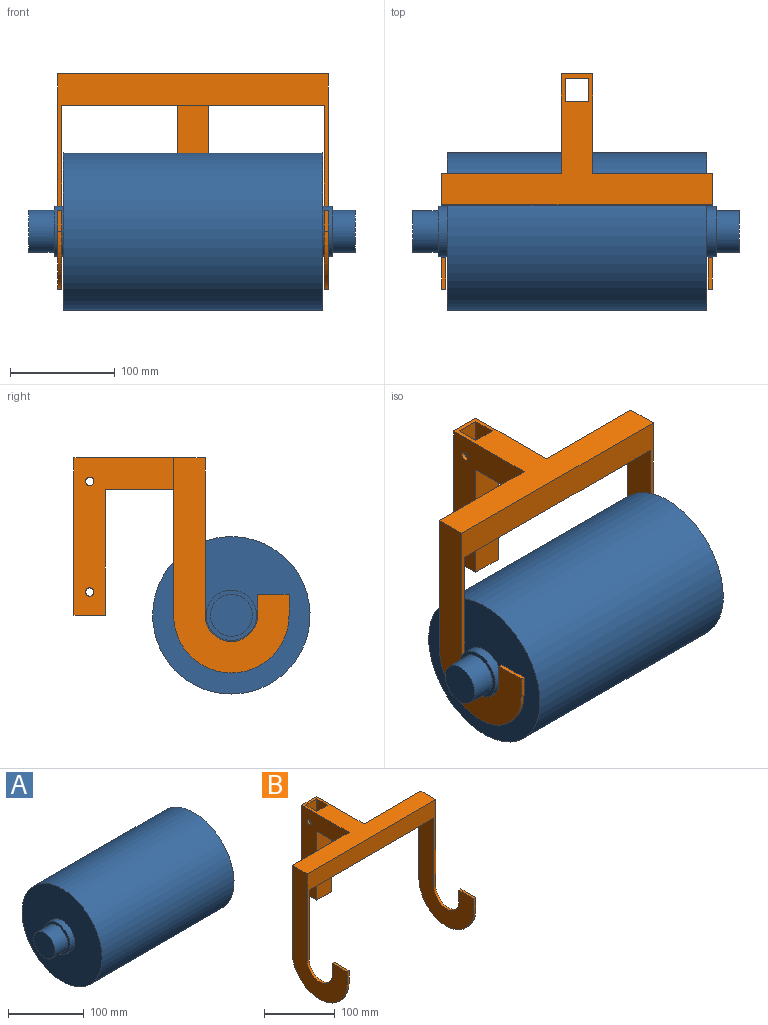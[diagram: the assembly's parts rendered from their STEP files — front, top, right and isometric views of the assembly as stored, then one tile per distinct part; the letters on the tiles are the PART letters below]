
ASSEMBLY  parts=2 mates=1
PART A: 11 faces, bbox 311x150x150 mm
  f0: cylinder r=75mm len=247mm, axis (-1,0,0), area 116396mm2, adj f1,f2
  f1: plane 150x150mm, normal (1,0,0), area 15861.9mm2, adj f0,f3
  f2: plane 150x150mm, normal (-1,0,0), area 15861.9mm2, adj f0,f7
  f3: cylinder r=24mm len=48mm, axis (-1,0,0), area 1357.2mm2, adj f1,f4
  f4: plane 48x48mm, normal (1,0,0), area 552.9mm2, adj f3,f5
  f5: cylinder r=20mm len=40mm, axis (-1,0,0), area 2764.6mm2, adj f4,f6
  f6: plane 40x40mm, normal (1,0,0), area 1256.6mm2, adj f5
  f7: cylinder r=24mm len=48mm, axis (1,0,0), area 1357.2mm2, adj f2,f8
  f8: plane 48x48mm, normal (-1,0,0), area 552.9mm2, adj f7,f9
  f9: cylinder r=20mm len=40mm, axis (1,0,0), area 3015.9mm2, adj f8,f10
  f10: plane 40x40mm, normal (-1,0,0), area 1256.6mm2, adj f9
PART B: 44 faces, bbox 258x205x205 mm
  f0: plane 150x114mm, normal (0,1,0), area 3900mm2, adj f7,f8,f9,f10,f11,f19
  f1: plane 150x114mm, normal (0,1,0), area 3900mm2, adj f8,f11,f12,f13,f14,f20
  f2: plane 258x150mm, normal (0,-1,0), area 8700mm2, adj f3,f8,f9,f10,f11,f12,f13,f18
  f3: cylinder r=25mm len=50mm, axis (1,0,0), area 314.2mm2, adj f2,f4,f9,f10
  f4: plane 20x4mm, normal (0,1,0), area 80mm2, adj f3,f5,f9,f10
  f5: plane 30x4mm, normal (0,0,1), area 120mm2, adj f4,f6,f9,f10
  f6: plane 20x4mm, normal (0,-1,0), area 80mm2, adj f5,f7,f9,f10
  f7: cylinder r=55mm len=110mm, axis (1,0,0), area 691.2mm2, adj f0,f6,f9,f10
  f8: plane 258x125mm, normal (0,0,1), area 10106mm2, adj f0,f1,f2,f9,f13,f19,f20,f21
  f9: plane 205x110mm, normal (-1,0,0), area 8869.9mm2, adj f0,f2,f3,f4,f5,f6,f7,f8
  f10: plane 175x110mm, normal (1,0,0), area 7969.9mm2, adj f0,f2,f3,f4,f5,f6,f7,f11
  f11: plane 250x95mm, normal (0,0,-1), area 9450mm2, adj f0,f1,f2,f10,f12,f19,f20,f26
  f12: plane 175x110mm, normal (-1,0,0), area 7969.9mm2, adj f1,f2,f11,f14,f15,f16,f17,f18
  f13: plane 205x110mm, normal (1,0,0), area 8869.9mm2, adj f1,f2,f8,f14,f15,f16,f17,f18
  f14: cylinder r=55mm len=110mm, axis (-1,0,0), area 691.2mm2, adj f1,f12,f13,f15
  f15: plane 20x4mm, normal (0,-1,0), area 80mm2, adj f12,f13,f14,f16
  f16: plane 30x4mm, normal (0,0,1), area 120mm2, adj f12,f13,f15,f17
  f17: plane 20x4mm, normal (0,1,0), area 80mm2, adj f12,f13,f16,f18
  f18: cylinder r=25mm len=50mm, axis (-1,0,0), area 314.2mm2, adj f2,f12,f13,f17
  f19: plane 150x95mm, normal (-1,0,0), area 6349.5mm2, adj f0,f8,f11,f23,f25,f26,f30,f31
  f20: plane 150x95mm, normal (1,0,0), area 6349.5mm2, adj f1,f8,f11,f23,f25,f26,f28,f29
  f21: plane 150x22mm, normal (1,0,0), area 3199.5mm2, adj f8,f23,f24,f27,f30,f31
  f22: plane 150x22mm, normal (-1,0,0), area 3199.5mm2, adj f8,f23,f24,f27,f28,f29
  f23: plane 30x30mm, normal (0,0,-1), area 416mm2, adj f19,f20,f21,f22,f24,f25,f26,f27
  f24: plane 150x22mm, normal (0,-1,0), area 3300mm2, adj f8,f21,f22,f23
  f25: plane 150x30mm, normal (0,1,0), area 4500mm2, adj f8,f19,f20,f23
  f26: plane 120x30mm, normal (0,-1,0), area 3600mm2, adj f11,f19,f20,f23
  f27: plane 150x22mm, normal (0,1,0), area 3300mm2, adj f8,f21,f22,f23
  f28: cylinder r=4mm len=8mm, axis (1,0,0), area 100.5mm2, adj f20,f22
  f29: cylinder r=4mm len=8mm, axis (1,0,0), area 100.5mm2, adj f20,f22
  f30: cylinder r=4mm len=8mm, axis (1,0,0), area 100.5mm2, adj f19,f21
  f31: cylinder r=4mm len=8mm, axis (1,0,0), area 100.5mm2, adj f19,f21
  f32: plane 22x22mm, normal (0,-1,0), area 484mm2, adj f33,f34,f35,f36
  f33: plane 65x22mm, normal (-1,0,0), area 1430mm2, adj f32,f34,f36,f37
  f34: plane 65x22mm, normal (0,0,1), area 1430mm2, adj f32,f33,f35,f37
  f35: plane 65x22mm, normal (1,0,0), area 1430mm2, adj f32,f34,f36,f37
  f36: plane 65x22mm, normal (0,0,-1), area 1430mm2, adj f32,f33,f35,f37
  f37: plane 22x22mm, normal (0,1,0), area 484mm2, adj f33,f34,f35,f36
  f38: plane 22x22mm, normal (1,0,0), area 484mm2, adj f39,f40,f41,f42
  f39: plane 250x22mm, normal (0,-1,0), area 5500mm2, adj f38,f40,f42,f43
  f40: plane 250x22mm, normal (0,0,-1), area 5500mm2, adj f38,f39,f41,f43
  f41: plane 250x22mm, normal (0,1,0), area 5500mm2, adj f38,f40,f42,f43
  f42: plane 250x22mm, normal (0,0,1), area 5500mm2, adj f38,f39,f41,f43
  f43: plane 22x22mm, normal (-1,0,0), area 484mm2, adj f39,f40,f41,f42
PLACE A t=(-539.89,195.33,993.34)mm
PLACE B rot(axis=(-0.15,-0.99,0),0deg) t=(-541.39,195.33,993.34)mm
MATE fastened A.f5 <-> B.f3  axis (-1,0,0) through (-572.89,195.33,993.34)mm
